# Revit family: BAS-IP_Вызывная панель_AV-04SDI
name_source: partatom
category: Устройства связи
units: mm (PartAtom-declared; Revit-internal decimal feet)

## family parameters
Всегда вертикально = Да
На основе рабочей плоскости = Нет
Общий = Нет
При загрузке вырезать с полостями = Нет
Размер круглого соединителя = Использовать диаметр
Сохранять ориентацию аннотаций = Нет
Тип детали = Нормальный
Точка расчета площади = Нет

## types (2) — shared parameters
ADSK_Единица измерения = шт.
ADSK_Завод-изготовитель = BAS-IP
ADSK_Количество = 1
ADSK_Наименование = Накладная индивидуальная панель с возможностью подключения индукционной петли
IK-код = IK07
Выходное видео = HD (1280 × 720), H.264 Main Profile
Дисплей = Нет
Изготовитель = BAS-IP
Камера = 1/4”
Класс степени защиты = IP65
Корпус = Алюминий
Минимальная освещенность = 0,01 Люкс
Ночная подсветка = 6 светодиодов
Питание = IEEE 803.2af PoE, +12 В постоянного тока
Потребление питания = 6,5 Вт, в режиме ожидания - 3,6 Вт
Размер под установку = 84.5 × 170 × 33 мм
Размер самой панели = 80 × 165 × 27 мм
Разрешение = 2 Мп
Температурный режим = -40 – +65 °С
Тип панели = Индивидуальная
Тип установки = Накладной монтаж. Накладка от солнца и дождя BR-AV04 (опционально)
Угол обзора камеры = 100° (по горизонтали)

## per-type parameters (varying)
| type | ADSK_Марка | ADSK_Материал |
| Серебристый | AV-04SDI Silver | Silver |
| Черный | AV-04SDI Black | Black silver |

note: column(s) folded — value = type name in every type: Цветовое решение
